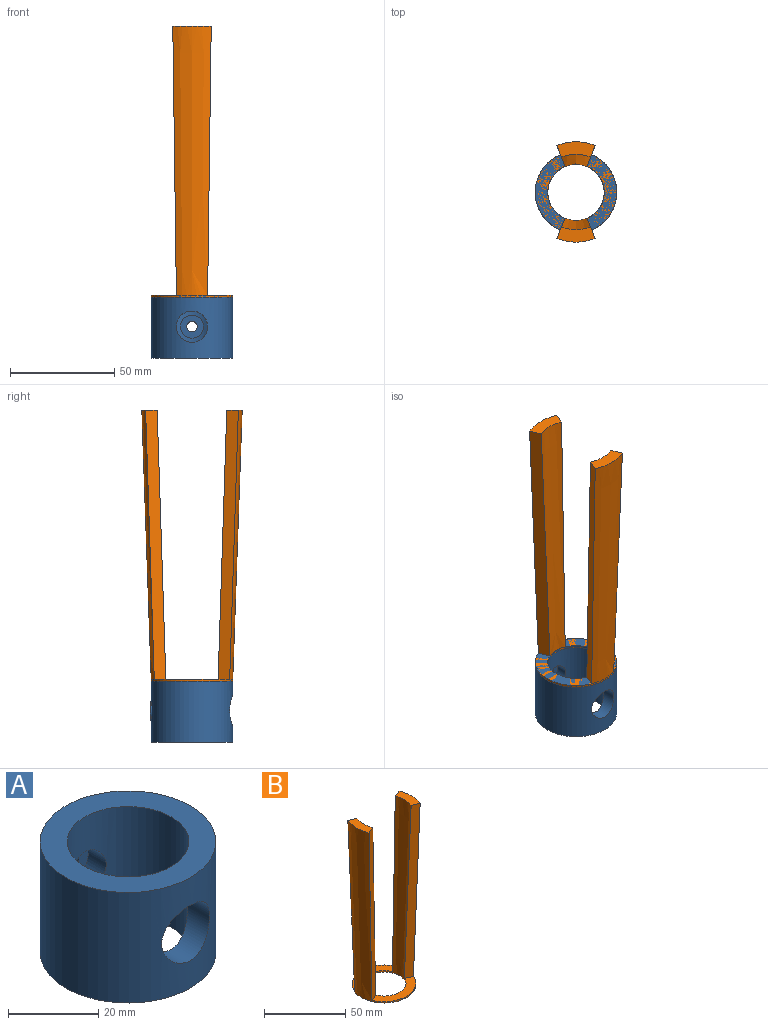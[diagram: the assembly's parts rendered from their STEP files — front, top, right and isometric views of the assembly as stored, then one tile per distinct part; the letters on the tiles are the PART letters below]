
ASSEMBLY  parts=2 mates=1
PART A: 10 faces, bbox 39x39.5x30 mm
  f0: cylinder r=19.5mm len=39mm, axis (0,0,-1), area 3431.3mm2, adj f2,f3,f4,f8
  f1: cylinder r=13.5mm len=30mm, axis (0,0,-1), area 2263.4mm2, adj f2,f3,f4,f5
  f2: plane 39x39mm, normal (0,0,1), area 622mm2, adj f0,f1
  f3: plane 39x39mm, normal (0,0,-1), area 622mm2, adj f0,f1
  f4: cylinder r=7.5mm len=15mm, axis (0,-1,0), area 300.1mm2, adj f0,f1
  f5: cylinder r=5.5mm len=11mm, axis (0,-1,0), area 175.5mm2, adj f1,f6
  f6: plane 11x11mm, normal (0,-1,0), area 75.4mm2, adj f5,f7
  f7: cylinder r=2.5mm len=5mm, axis (0,1,0), area 31.4mm2, adj f6,f9
  f8: cylinder r=4.5mm len=9mm, axis (0,1,0), area 21.6mm2, adj f0,f9
  f9: plane 9x9mm, normal (0,1,0), area 44mm2, adj f7,f8
PART B: 11 faces, bbox 48.1x48.1x130 mm
  f0: plane 36.1x14.36mm, normal (0,0,1), area 233.8mm2, adj f1,f4,f7,f10
  f1: cone r=19.5mm half-angle=2deg, axis (0,0,1), area 4540.2mm2, adj f0,f2,f3,f4,f5,f6,f7,f8
  f2: plane 36.1x14.36mm, normal (0,0,1), area 233.8mm2, adj f1,f5,f8,f10
  f3: plane 39x39mm, normal (0,0,-1), area 622mm2, adj f1,f10
  f4: plane 129x9.71mm, normal (0.38,0.92,0), area 774mm2, adj f0,f1,f6,f10
  f5: plane 129x9.71mm, normal (0.38,-0.92,0), area 774mm2, adj f1,f2,f6,f10
  f6: plane 18.4x7.37mm, normal (0,0,1), area 99.1mm2, adj f1,f4,f5,f10
  f7: plane 129x9.71mm, normal (-0.38,0.92,0), area 774mm2, adj f0,f1,f9,f10
  f8: plane 129x9.71mm, normal (-0.38,-0.92,0), area 774mm2, adj f1,f2,f9,f10
  f9: plane 18.4x7.37mm, normal (0,0,1), area 99.1mm2, adj f1,f7,f8,f10
  f10: cone r=18.04mm half-angle=2deg, axis (0,0,1), area 3286mm2, adj f0,f2,f3,f4,f5,f6,f7,f8
PLACE A t=(21.86,20.29,-29)mm
PLACE B rot(axis=(0,0,-1),90deg) t=(21.86,20.29,0)mm
MATE fastened A.f1 <-> B.f1  axis (0,0,-1) through (21.86,20.29,1)mm
